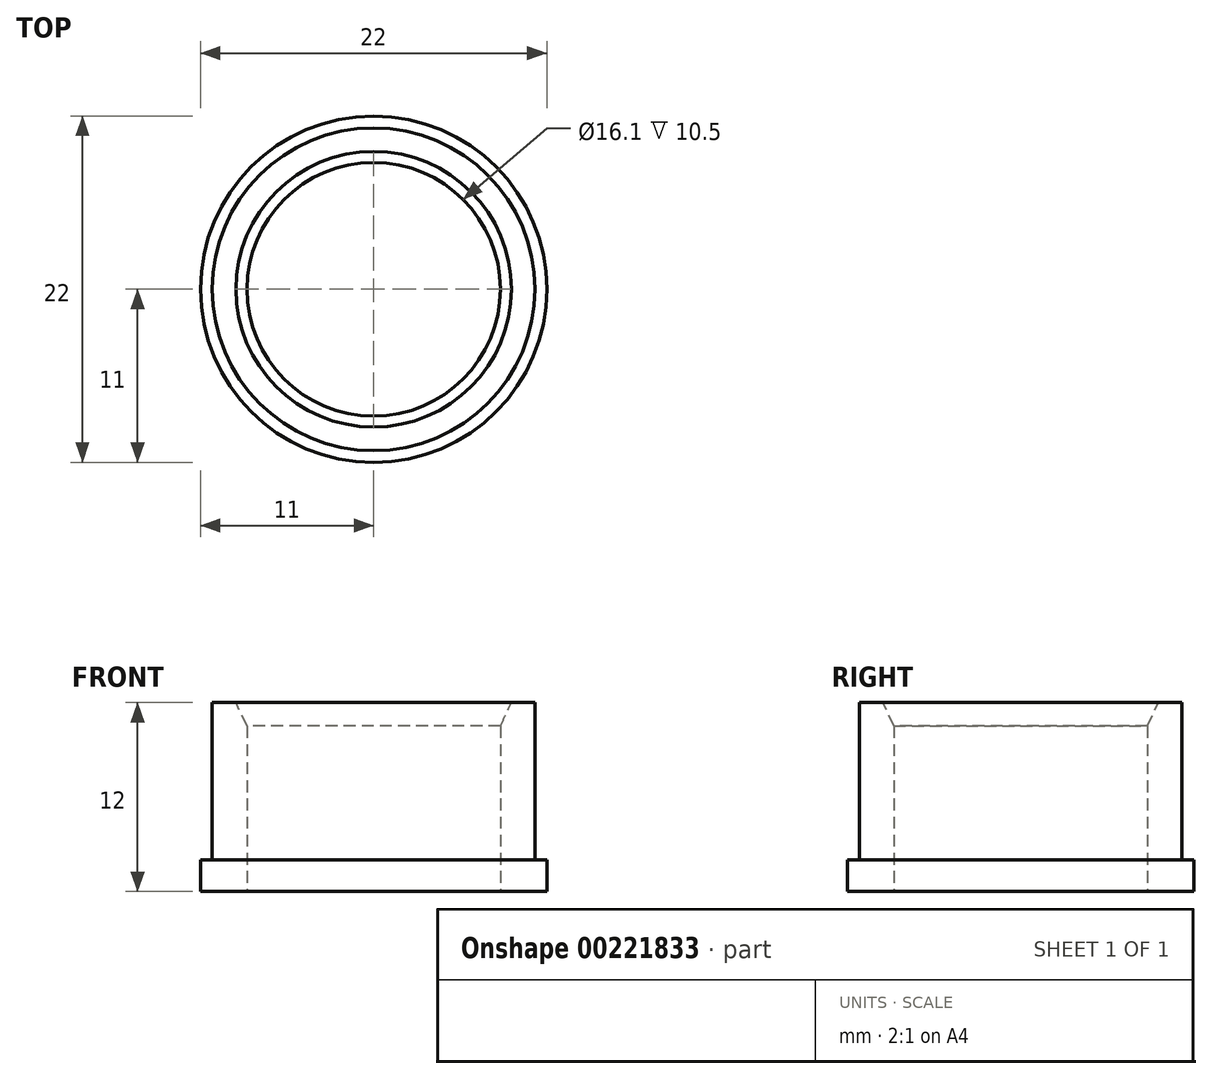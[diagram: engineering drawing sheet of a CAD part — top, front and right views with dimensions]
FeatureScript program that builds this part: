
annotation { "Feature Type Name" : "Feature", "Feature Type Description" : "" }
export const myFeature = defineFeature(function(context is Context, id is Id, definition is map)
    precondition{}
    {
        {
            var Q0;
            Q0=qCreatedBy(makeId("Top.planeOp"),FACE);
            var sketch = newSketch(context, id + "F0", { "sketchPlane" : qUnion([Q0])});
            skCircle(sketch, "E0", {"center": v(0, 0) * mm, "radius": 11 * mm});
            skCircle(sketch, "E1", {"center": v(0, 0) * mm, "radius": 8.05 * mm});
            skSolve(sketch);
        }
        {
            var Q0;
            Q0 = qSketchRegion(id + "F0", true);
            extrude(context, id + "F1", {"entities" : qUnion([Q0]), "depth" : 2 * mm});
        }
        {
            var Q0;
            Q0=makeQuery(id+"F1.opExtrude","CAP_FACE",FACE,{"disambiguationData":[OSD([sQuery(id+"F0.wireOp",EDGE,"E0"),sQuery(id+"F0.wireOp",EDGE,"E1")])],"isStart":false});
            var sketch = newSketch(context, id + "F2", { "sketchPlane" : qUnion([Q0])});
            skCircle(sketch, "E2.0", {"center": v(0, 0) * mm, "radius": 8.05 * mm});
            skCircle(sketch, "E3", {"center": v(0, 0) * mm, "radius": 10.25 * mm});
            skSolve(sketch);
        }
        {
            var Q0;
            Q0 = qSketchRegion(id + "F2", true);
            extrude(context, id + "F3", {"entities" : qUnion([Q0]), "operationType" : NewBodyOperationType.ADD, "depth" : 10 * mm});
        }
        {
            var Q0;
            Q0=makeQuery(id+"F3.opExtrude","CAP_EDGE",EDGE,{"disambiguationData":[OSD([sQuery(id+"F2.wireOp",EDGE,"E2.0")])],"isStart":false});
            chamfer(context, id + "F4", {"entities" : qUnion([Q0]), "chamferType" : ChamferType.OFFSET_ANGLE, "width" : 1.5 * mm, "oppositeDirection" : false, "angle" : 25 * degree, "tangentPropagation" : true});
        }
    });
